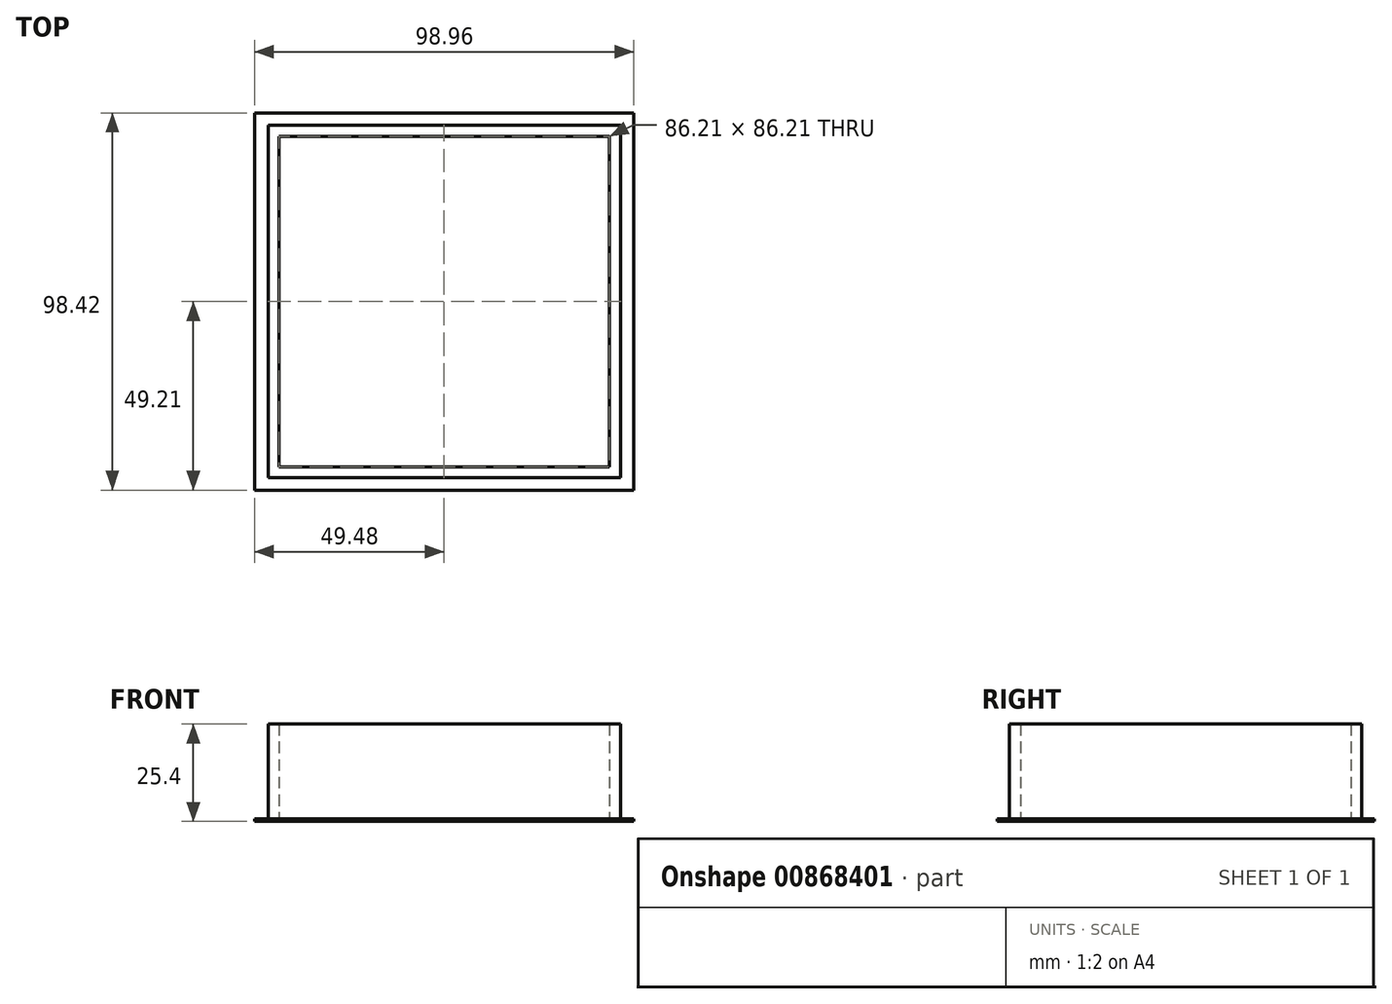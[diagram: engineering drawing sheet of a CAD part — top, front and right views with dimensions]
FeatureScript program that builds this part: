
annotation { "Feature Type Name" : "Feature", "Feature Type Description" : "" }
export const myFeature = defineFeature(function(context is Context, id is Id, definition is map)
    precondition{}
    {
        {
            var Q0;
            Q0=qCreatedBy(makeId("Top.planeOp"),FACE);
            var sketch = newSketch(context, id + "F0", { "sketchPlane" : qUnion([Q0])});
            skLineSegment(sketch, "E0.bottom", {"start": v(-45.97, 45.99) * mm, "end": v(45.97, 45.99) * mm});
            skLineSegment(sketch, "E0.top", {"start": v(-45.97, -45.99) * mm, "end": v(45.97, -45.99) * mm});
            skLineSegment(sketch, "E0.left", {"start": v(-45.97, 45.99) * mm, "end": v(-45.97, -45.99) * mm});
            skLineSegment(sketch, "E0.right", {"start": v(45.97, 45.99) * mm, "end": v(45.97, -45.99) * mm});
            skPoint(sketch, "E0.middle", {"position": v(0, 0) * mm});
            skLineSegment(sketch, "E1.bottom", {"start": v(43.1, 43.1) * mm, "end": v(-43.1, 43.1) * mm});
            skLineSegment(sketch, "E1.top", {"start": v(43.1, -43.1) * mm, "end": v(-43.1, -43.1) * mm});
            skLineSegment(sketch, "E1.left", {"start": v(43.1, 43.1) * mm, "end": v(43.1, -43.1) * mm});
            skLineSegment(sketch, "E1.right", {"start": v(-43.1, 43.1) * mm, "end": v(-43.1, -43.1) * mm});
            skSolve(sketch);
        }
        {
            var Q0;
            Q0=makeQuery(id+"F0.imprint","IMPRINT",FACE,{"disambiguationData":[TD([[makeQuery(id+"F0.imprint","IMPRINT",EDGE,{"derivedFrom":sQuery(id+"F0.wireOp",EDGE,"E0.bottom")}),-1.0]])]});
            extrude(context, id + "F1", {"entities" : qUnion([Q0]), "depth" : 25.4 * mm, "offsetDistance" : 25.4 * mm});
        }
        {
            var Q0;
            Q0=qCreatedBy(makeId("Top.planeOp"),FACE);
            var sketch = newSketch(context, id + "F2", { "sketchPlane" : qUnion([Q0])});
            skLineSegment(sketch, "E2.bottom", {"start": v(-49.48, 49.21) * mm, "end": v(49.48, 49.21) * mm});
            skLineSegment(sketch, "E2.top", {"start": v(-49.48, -49.21) * mm, "end": v(49.48, -49.21) * mm});
            skLineSegment(sketch, "E2.left", {"start": v(-49.48, 49.21) * mm, "end": v(-49.48, -49.21) * mm});
            skLineSegment(sketch, "E2.right", {"start": v(49.48, 49.21) * mm, "end": v(49.48, -49.21) * mm});
            skPoint(sketch, "E2.middle", {"position": v(0, 0) * mm});
            skLineSegment(sketch, "E3.bottom", {"start": v(-45.81, 45.94) * mm, "end": v(45.81, 45.94) * mm});
            skLineSegment(sketch, "E3.top", {"start": v(-45.81, -45.94) * mm, "end": v(45.81, -45.94) * mm});
            skLineSegment(sketch, "E3.left", {"start": v(-45.81, 45.94) * mm, "end": v(-45.81, -45.94) * mm});
            skLineSegment(sketch, "E3.right", {"start": v(45.81, 45.94) * mm, "end": v(45.81, -45.94) * mm});
            skSolve(sketch);
        }
        {
            var Q0;
            Q0=makeQuery(id+"F2.imprint","IMPRINT",FACE,{"disambiguationData":[TD([[makeQuery(id+"F2.imprint","IMPRINT",EDGE,{"derivedFrom":sQuery(id+"F2.wireOp",EDGE,"E2.bottom")}),-1.0]])]});
            extrude(context, id + "F3", {"entities" : qUnion([Q0]), "operationType" : NewBodyOperationType.ADD, "depth" : 0.64 * mm, "offsetDistance" : 25.4 * mm});
        }
    });
